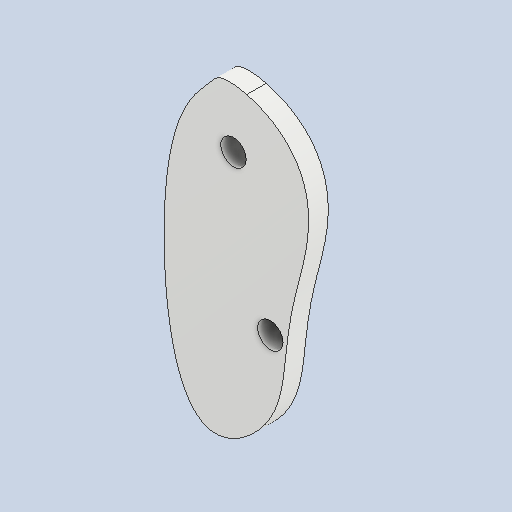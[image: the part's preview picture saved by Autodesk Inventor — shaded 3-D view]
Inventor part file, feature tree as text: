
AUTODESK INVENTOR PART (.ipt)
format: ipt  version: 2022 (Build 260153000, 153)  size: 112,640 bytes
history: native  units: in
note: dims shown in document units (in); Inventor stores cm internally (conversion verified against a paired STEP export)
features: other x3, sketch x2
ambient origin geometry x8: Origin, YZ Plane, XZ Plane, XY Plane, X Axis, Y Axis, Z Axis, Center Point
bodies: Solid1 (feature_tree)
feature tree (5):
  other  "Component35.ipt"
  other  "Solid1::Component35.ipt"
  other  "TaggingFeature1"
  sketch  "Sketch2"  dims[d0=0.3937in]
  sketch  "Sketch3"
